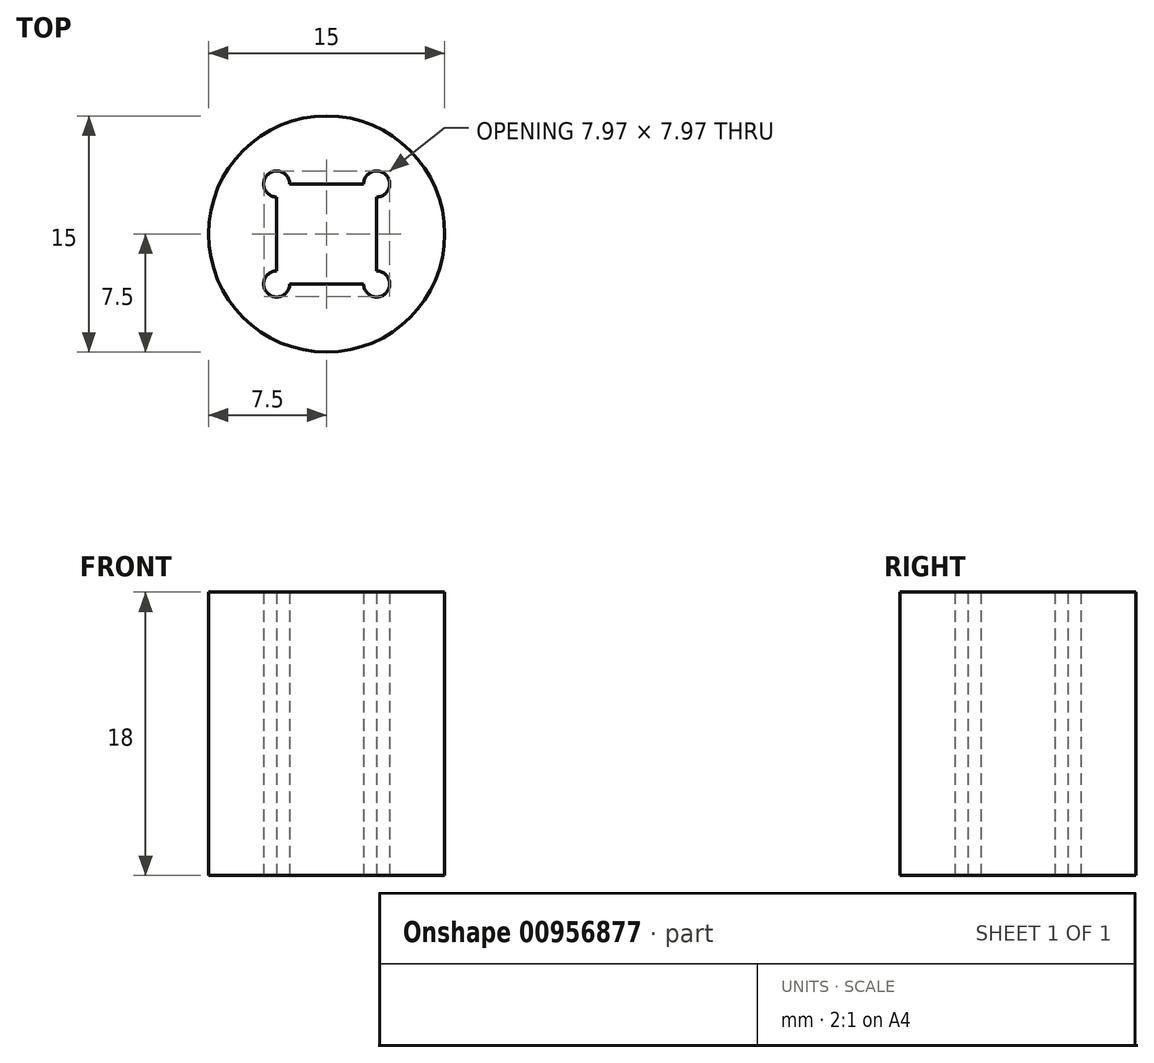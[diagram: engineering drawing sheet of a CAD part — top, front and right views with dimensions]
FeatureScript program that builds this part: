
annotation { "Feature Type Name" : "Feature", "Feature Type Description" : "" }
export const myFeature = defineFeature(function(context is Context, id is Id, definition is map)
    precondition{}
    {
        {
            var Q0;
            Q0=qCreatedBy(makeId("Top.planeOp"),FACE);
            var sketch = newSketch(context, id + "F0", { "sketchPlane" : qUnion([Q0])});
            skCircle(sketch, "E0", {"center": v(0, 0) * mm, "radius": 7.5 * mm});
            skLineSegment(sketch, "E1.bottom", {"start": v(2.35, -3.18) * mm, "end": v(-2.35, -3.18) * mm});
            skLineSegment(sketch, "E1.top", {"start": v(2.35, 3.18) * mm, "end": v(-2.35, 3.18) * mm});
            skLineSegment(sketch, "E1.left", {"start": v(3.18, -2.35) * mm, "end": v(3.18, 2.35) * mm});
            skLineSegment(sketch, "E1.right", {"start": v(-3.17, -2.35) * mm, "end": v(-3.17, 2.35) * mm});
            skArc(sketch, "E2", {"start": v(3.18, 2.35) * mm, "mid": v(3.76, 3.76) * mm, "end": v(2.35, 3.18) * mm});
            skArc(sketch, "E3", {"start": v(-2.35, 3.18) * mm, "mid": v(-3.76, 3.76) * mm, "end": v(-3.17, 2.35) * mm});
            skArc(sketch, "E4", {"start": v(-3.18, -2.35) * mm, "mid": v(-3.76, -3.76) * mm, "end": v(-2.35, -3.18) * mm});
            skArc(sketch, "E5", {"start": v(2.35, -3.18) * mm, "mid": v(3.76, -3.76) * mm, "end": v(3.18, -2.35) * mm});
            skSolve(sketch);
        }
        {
            var Q0;
            Q0=makeQuery(id+"F0.imprint","IMPRINT",FACE,{"disambiguationData":[TD([[makeQuery(id+"F0.imprint","IMPRINT",EDGE,{"derivedFrom":sQuery(id+"F0.wireOp",EDGE,"E0")}),1.0]])]});
            extrude(context, id + "F1", {"entities" : qUnion([Q0]), "depth" : 18 * mm, "offsetDistance" : 25.4 * mm});
        }
    });
